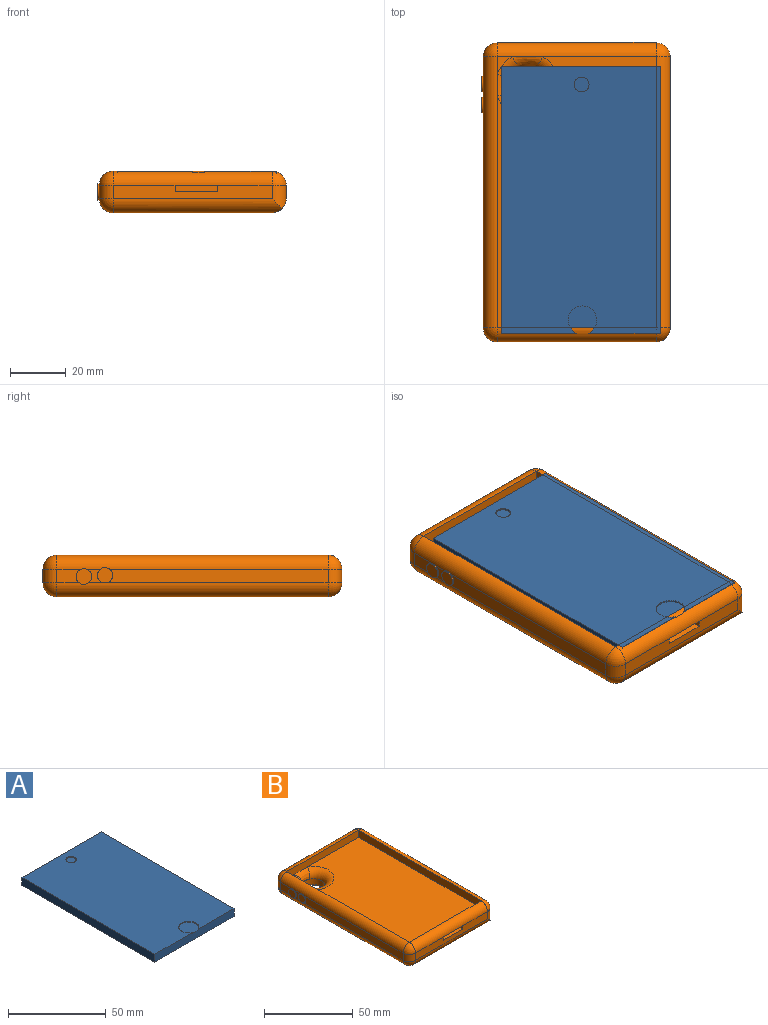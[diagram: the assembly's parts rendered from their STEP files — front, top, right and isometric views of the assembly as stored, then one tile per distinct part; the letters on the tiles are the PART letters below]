
ASSEMBLY  parts=2 mates=1
PART A: 10 faces, bbox 57.3x96.2x5 mm
  f0: plane 96.16x5mm, normal (1,0,0), area 480.8mm2, adj f1,f3,f4,f5
  f1: plane 57.27x5mm, normal (0,1,0), area 286.4mm2, adj f0,f2,f4,f5
  f2: plane 96.16x5mm, normal (-1,0,0), area 480.8mm2, adj f1,f3,f4,f5
  f3: plane 57.27x5mm, normal (0,-1,0), area 284.2mm2, adj f0,f2,f4,f5,f6,f7
  f4: plane 96.16x57.27mm, normal (0,0,1), area 5403.3mm2, adj f0,f1,f2,f3,f7,f8
  f5: plane 96.16x57.27mm, normal (0,0,-1), area 5507.4mm2, adj f0,f1,f2,f3
  f6: plane 10.31x9.84mm, normal (0,0,1), area 82.1mm2, adj f3,f7
  f7: cylinder r=5.15mm len=10.31mm, axis (0,0,1), area 14mm2, adj f3,f4,f6
  f8: cylinder r=2.65mm len=5.3mm, axis (0,0,1), area 8.3mm2, adj f4,f9
  f9: plane 5.3x5.3mm, normal (0,0,1), area 22mm2, adj f8
PART B: 63 faces, bbox 67.9x108.1x15.2 mm
  f0: plane 6.8x5mm, normal (-1,0,0), area 15mm2, adj f10,f14,f46,f50
  f1: plane 80.27x5mm, normal (-1,0,0), area 390mm2, adj f10,f14,f16,f50
  f2: plane 6.3x5.45mm, normal (0,0,1), area 12.9mm2, adj f24,f27,f40
  f3: plane 44.72x5mm, normal (0,1,0), area 223.6mm2, adj f11,f20,f22,f36
  f4: plane 97.64x57.27mm, normal (0,0,1), area 5108.8mm2, adj f24,f25,f26,f27,f29,f31,f33,f41
  f5: plane 8.9x5mm, normal (-1,0,0), area 36.8mm2, adj f10,f14,f22,f46
  f6: plane 57.27x5mm, normal (0,-1,0), area 252.9mm2, adj f12,f16,f18,f29,f30,f31,f58
  f7: plane 97.64x5mm, normal (1,0,0), area 488.2mm2, adj f13,f19,f58,f61
  f8: plane 6.48x5mm, normal (0,1,0), area 12.7mm2, adj f11,f20,f59,f61
  f9: plane 97.64x57.27mm, normal (0,0,-1), area 5318.2mm2, adj f14,f18,f19,f20,f38,f43,f52,f53
  f10: cylinder r=5mm len=97.64mm, axis (0,1,0), area 766.8mm2, adj f0,f1,f5,f15,f23,f24,f45,f49
  f11: cylinder r=5mm len=57.27mm, axis (1,0,0), area 449.8mm2, adj f3,f8,f23,f27,f34,f60
  f12: cylinder r=5mm len=57.27mm, axis (-1,0,0), area 449.8mm2, adj f6,f15,f25,f32,f57
  f13: cylinder r=5mm len=97.64mm, axis (0,-1,0), area 766.8mm2, adj f7,f26,f57,f60
  f14: cylinder r=5mm len=97.64mm, axis (0,-1,0), area 766.8mm2, adj f0,f1,f5,f9,f17,f21,f48
  f15: sphere r=5mm, area 39.3mm2, adj f10,f12,f16
  f16: cylinder r=5mm len=5mm, axis (0,0,-1), area 39.3mm2, adj f1,f6,f15,f17
  f17: sphere r=5mm, area 39.3mm2, adj f14,f16,f18
  f18: cylinder r=5mm len=60.81mm, axis (1,0,0), area 463.7mm2, adj f6,f9,f17,f19,f58
  f19: cylinder r=5mm len=101.17mm, axis (0,1,0), area 780.7mm2, adj f7,f9,f18,f58,f62
  f20: cylinder r=5mm len=57.27mm, axis (-1,0,0), area 449.8mm2, adj f3,f8,f9,f21,f35,f62
  f21: sphere r=5mm, area 39.3mm2, adj f14,f20,f22
  f22: cylinder r=5mm len=5mm, axis (0,0,1), area 39.3mm2, adj f3,f5,f21,f23
  f23: sphere r=5mm, area 39.3mm2, adj f10,f11,f22
  f24: plane 97.71x5.08mm, normal (1,0,0), area 488.2mm2, adj f2,f4,f10,f25,f27,f42
  f25: plane 57.27x5mm, normal (0,1,0), area 286.4mm2, adj f4,f12,f24,f26,f32
  f26: plane 97.64x5mm, normal (-1,0,0), area 488.2mm2, adj f4,f13,f25,f27
  f27: plane 57.45x5.17mm, normal (0,-1,0), area 286.4mm2, adj f2,f4,f11,f24,f26,f39
  f28: cylinder r=6.61mm len=13.21mm, axis (0,0,-1), area 170.2mm2, adj f38,f39,f40,f41,f42
  f29: plane 9x2.2mm, normal (1,0,0), area 19.8mm2, adj f4,f6,f30,f32,f33
  f30: plane 15.22x9mm, normal (0,0,1), area 137mm2, adj f6,f29,f31,f33
  f31: plane 9x2.2mm, normal (-1,0,0), area 19.8mm2, adj f4,f6,f30,f32,f33
  f32: plane 15.22x5mm, normal (0,0,-1), area 76.1mm2, adj f12,f25,f29,f31
  f33: plane 15.22x2.2mm, normal (0,-1,0), area 33.5mm2, adj f4,f29,f30,f31
  f34: plane 6.08x0.3mm, normal (0,0,1), area 1.8mm2, adj f11,f36,f37,f59
  f35: plane 11.08x0.3mm, normal (0,0,-1), area 3.3mm2, adj f20,f36,f37,f59
  f36: plane 5x0.3mm, normal (-1,0,0), area 1.5mm2, adj f3,f34,f35,f37
  f37: plane 11.08x5mm, normal (0,1,0), area 50mm2, adj f34,f35,f36,f59
  f38: torus R=7.51mm, axis (0,0,1), area 61.6mm2, adj f9,f28
  f39: bspline ~12x5.25mm, area 54.8mm2, adj f27,f28,f40,f41
  f40: torus R=11.61mm, axis (0,0,1), area 48.6mm2, adj f2,f28,f39,f42
  f41: torus R=11.61mm, axis (0,0,1), area 256.4mm2, adj f4,f28,f39,f42
  f42: bspline ~8.78x5.19mm, area 42.1mm2, adj f24,f28,f40,f41
  f43: cylinder r=2.16mm len=4.32mm, axis (0,0,-1), area 6.8mm2, adj f9,f44
  f44: plane 4.32x4.32mm, normal (0,0,-1), area 14.6mm2, adj f43
  f45: plane 1.67x0.13mm, normal (1,0,0), area 0.1mm2, adj f10,f46
  f46: cylinder r=2.82mm len=5.64mm, axis (1,0,0), area 8.9mm2, adj f0,f5,f45,f47,f48
  f47: plane 5.64x5.64mm, normal (-1,0,0), area 25mm2, adj f46
  f48: plane 3.25x0.52mm, normal (1,0,0), area 1.1mm2, adj f14,f46
  f49: plane 3.17x0.5mm, normal (1,0,0), area 1.1mm2, adj f10,f50
  f50: cylinder r=2.75mm len=5.5mm, axis (1,0,0), area 8.6mm2, adj f0,f1,f49,f51
  f51: plane 5.5x5.5mm, normal (-1,0,0), area 23.8mm2, adj f50
  f52: plane 2.18x0.9mm, normal (-1,0,0), area 2mm2, adj f9,f53,f55,f56
  f53: plane 37.72x0.9mm, normal (0,1,0), area 33.9mm2, adj f9,f52,f54,f56
  f54: plane 2.18x0.9mm, normal (1,0,0), area 2mm2, adj f9,f53,f55,f56
  f55: plane 37.72x0.9mm, normal (0,-1,0), area 33.9mm2, adj f9,f52,f54,f56
  f56: plane 37.72x2.18mm, normal (0,0,-1), area 82.2mm2, adj f52,f53,f54,f55
  f57: sphere r=5mm, area 39.3mm2, adj f12,f13,f58
  f58: cylinder r=5mm len=8.54mm, axis (0,0,1), area 53.2mm2, adj f6,f7,f18,f19,f57
  f59: cylinder r=5mm len=5mm, axis (0,-1,0), area 2.4mm2, adj f8,f34,f35,f37
  f60: sphere r=5mm, area 39.3mm2, adj f11,f13,f61
  f61: cylinder r=5mm len=5mm, axis (0,0,-1), area 39.3mm2, adj f7,f8,f60,f62
  f62: sphere r=5mm, area 39.3mm2, adj f19,f20,f61
PLACE A t=(-13.99,21.39,5.6)mm
PLACE B t=(-15.45,23.29,5.6)mm
MATE fastened A.f5 <-> B.f4  axis (0,0,-1) through (-17.61,9.01,15.6)mm
